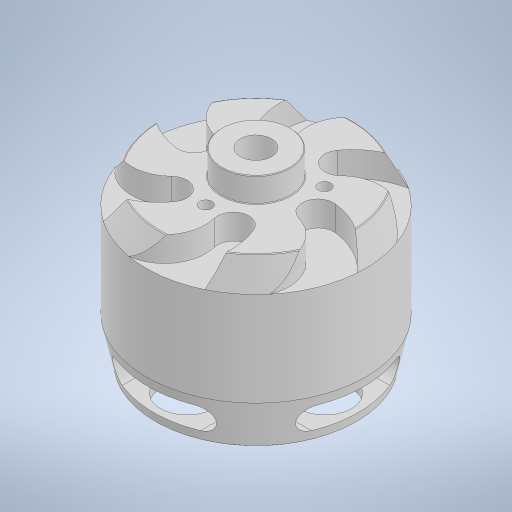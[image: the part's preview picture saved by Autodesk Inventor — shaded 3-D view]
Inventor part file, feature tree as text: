
AUTODESK INVENTOR PART (.ipt)
format: ipt  version: 2023.2 (Build 272271000, 271)  size: 433,152 bytes
history: native  units: in
note: dims shown in document units (in); Inventor stores cm internally (conversion verified against a paired STEP export)
features: sketch x4, extrude x3, revolve x1, chamfer x1, pattern_circular x1
ambient origin geometry x8: Origin, YZ Plane, XZ Plane, XY Plane, X Axis, Y Axis, Z Axis, Center Point
bodies: Solid1 (feature_tree)
feature tree (10):
  revolve  "Revolution1"  [1 undecoded]
  chamfer  "Chamfer1"  Distance=0.6004in
  extrude  "Extrusion1"  Depth=0.0787in
  extrude  "Extrusion2"  Depth=0.0787in
  extrude  "Extrusion3"  Depth=0.0787in
  pattern_circular  "Circular Pattern1"  Angle=90.0deg  [1 undecoded]
  sketch  "Sketch1"  dims[d0=1.1772in d1=0.6299in]
  sketch  "Sketch2"  dims[d2=0.689in]
  sketch  "Sketch3"  dims[d3=0.2756in]
  sketch  "Sketch4"  dims[d4=0.8661in d5=0.6004in d6=0.1575in d7=0.2165in d8=0.0984in d9=90.0deg d10=0.0039in d11=0.125in d12=45.0deg d13=0.6299in d14=0.0787in d15=1.1811in d17=360.0deg d19=0.5807in d21=0.1969in d22=1.378in d23=1.2008in d24=0.1969in d26=30.0deg d27=0.2559in d28=0.4528in d29=2.3622in d31=360.0deg d33=0.1575in d34=0.0in d35=0.8661in d36=0.748in d37=0.9843in d38=0.3346in d39=1.5748in d41=360.0deg d43=45.0deg d44=0.1181in d45=0.1181in d46=0.7874in d48=360.0deg d50=0.0591in d51=0.0in d52=0.4921in d53=0.0787in d54=0.0591in d55=0.0in d56=0.0in d57=0.7874in d58=90.0deg]
note: 2 required parameter values undecoded (feature->parameter linkage not recoverable at this tier; creation-order binding heuristic only, values carry confidence <= 0.55)